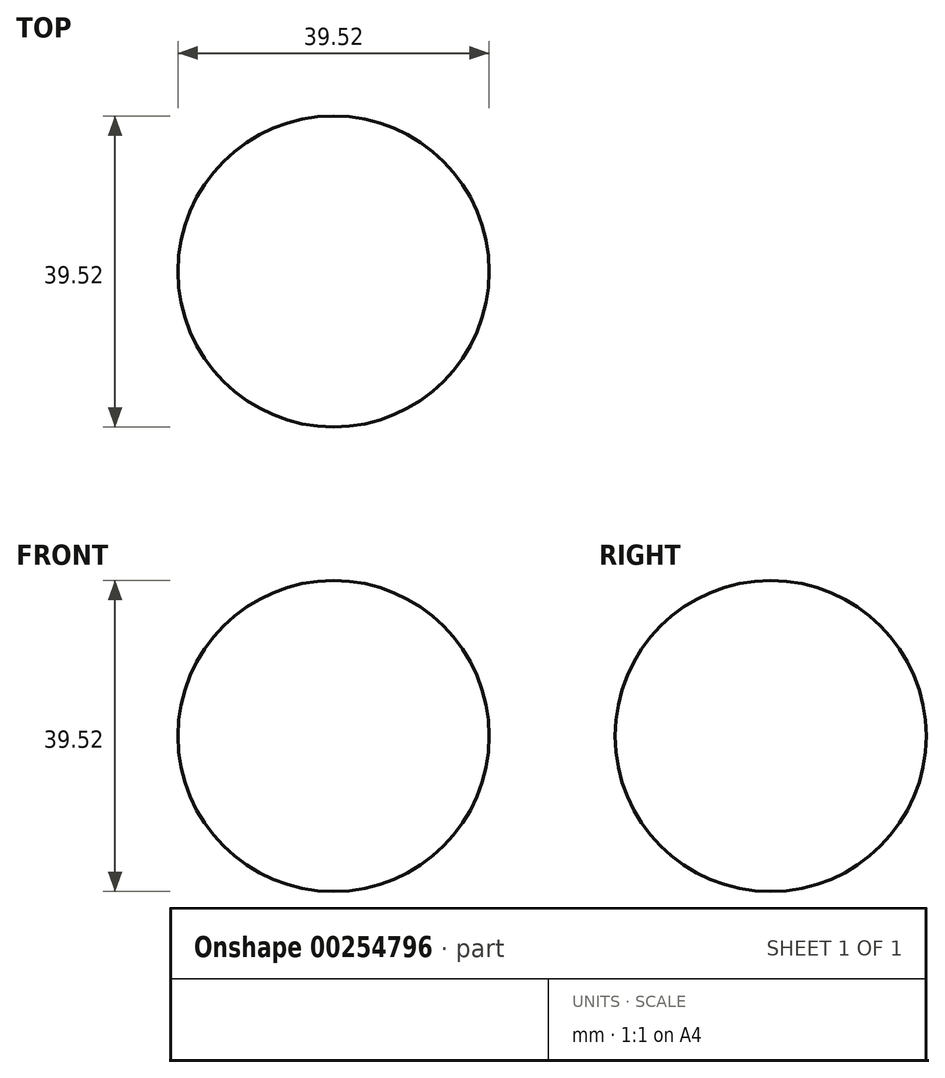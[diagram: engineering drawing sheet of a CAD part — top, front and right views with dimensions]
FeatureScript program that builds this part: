
annotation { "Feature Type Name" : "Feature", "Feature Type Description" : "" }
export const myFeature = defineFeature(function(context is Context, id is Id, definition is map)
    precondition{}
    {
        {
            var Q0;
            Q0=qCreatedBy(makeId("Front.planeOp"),FACE);
            var sketch = newSketch(context, id + "F0", { "sketchPlane" : qUnion([Q0])});
            skLineSegment(sketch, "E0", {"start": v(0, 0) * mm, "end": v(0, 39.52) * mm});
            skArc(sketch, "E1", {"start": v(0, 39.52) * mm, "mid": v(19.76, 19.76) * mm, "end": v(0, 0) * mm});
            skSolve(sketch);
        }
        {
            var Q0;
            Q0 = qSketchRegion(id + "F0", true);
            var Q1;
            Q1=sQuery(id+"F0.wireOp",EDGE,"E0");
            revolve(context, id + "F1", {"entities" : qUnion([Q0]), "axis" : qUnion([Q1]), "revolveType" : RevolveType.FULL});
        }
    });
